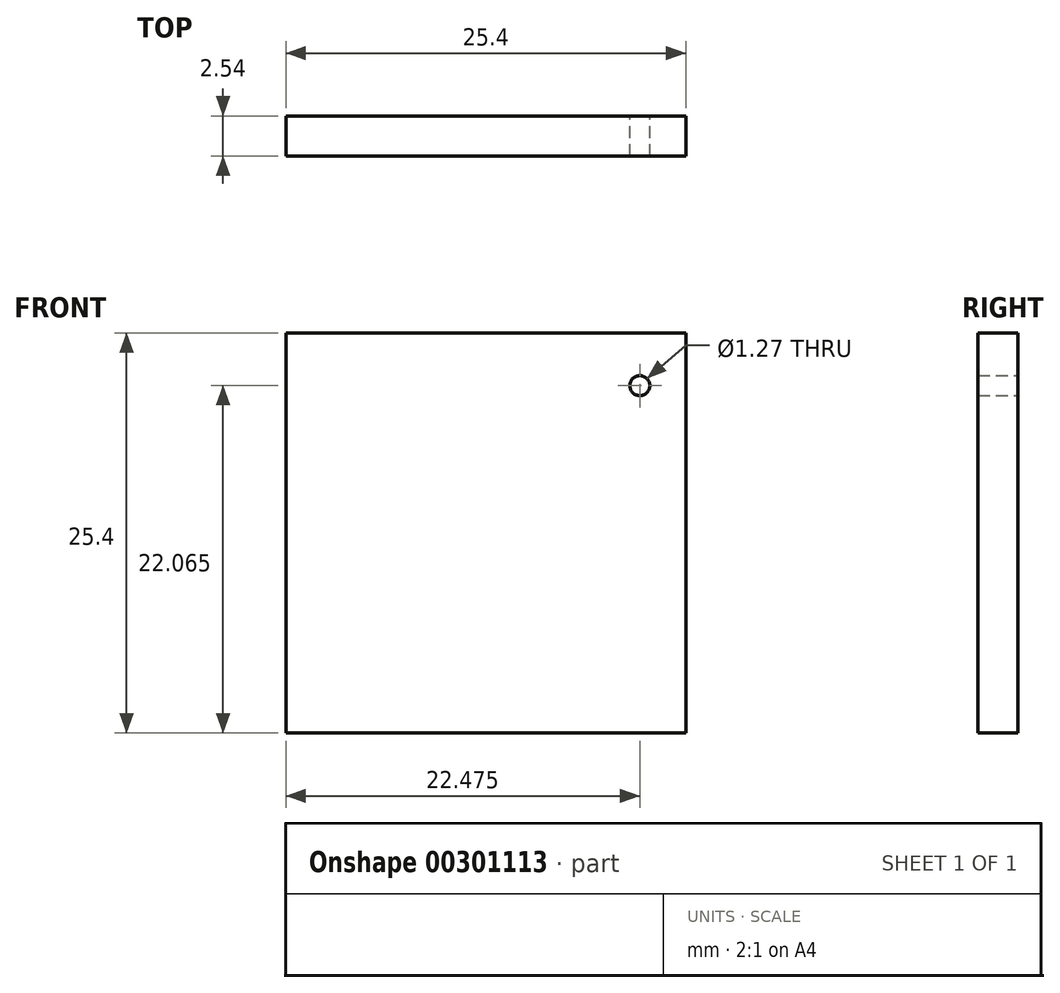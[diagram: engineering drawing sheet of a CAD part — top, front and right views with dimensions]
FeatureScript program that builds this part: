
annotation { "Feature Type Name" : "Feature", "Feature Type Description" : "" }
export const myFeature = defineFeature(function(context is Context, id is Id, definition is map)
    precondition{}
    {
        {
            var Q0;
            Q0=qCreatedBy(makeId("Front.planeOp"),FACE);
            var sketch = newSketch(context, id + "F0", { "sketchPlane" : qUnion([Q0])});
            skLineSegment(sketch, "E0.bottom", {"start": v(-12.7, -12.7) * mm, "end": v(12.7, -12.7) * mm});
            skLineSegment(sketch, "E0.top", {"start": v(-12.7, 12.7) * mm, "end": v(12.7, 12.7) * mm});
            skLineSegment(sketch, "E0.left", {"start": v(-12.7, -12.7) * mm, "end": v(-12.7, 12.7) * mm});
            skLineSegment(sketch, "E0.right", {"start": v(12.7, -12.7) * mm, "end": v(12.7, 12.7) * mm});
            skPoint(sketch, "E0.middle", {"position": v(0, 0) * mm});
            skCircle(sketch, "E1", {"center": v(9.78, 9.36) * mm, "radius": 0.64 * mm});
            skSolve(sketch);
        }
        {
            var Q0;
            Q0=makeQuery(id+"F0.imprint","IMPRINT",FACE,{"disambiguationData":[TD([[makeQuery(id+"F0.imprint","IMPRINT",EDGE,{"derivedFrom":sQuery(id+"F0.wireOp",EDGE,"E0.bottom")}),1.0]])]});
            extrude(context, id + "F1", {"entities" : qUnion([Q0]), "depth" : 2.54 * mm});
        }
    });
